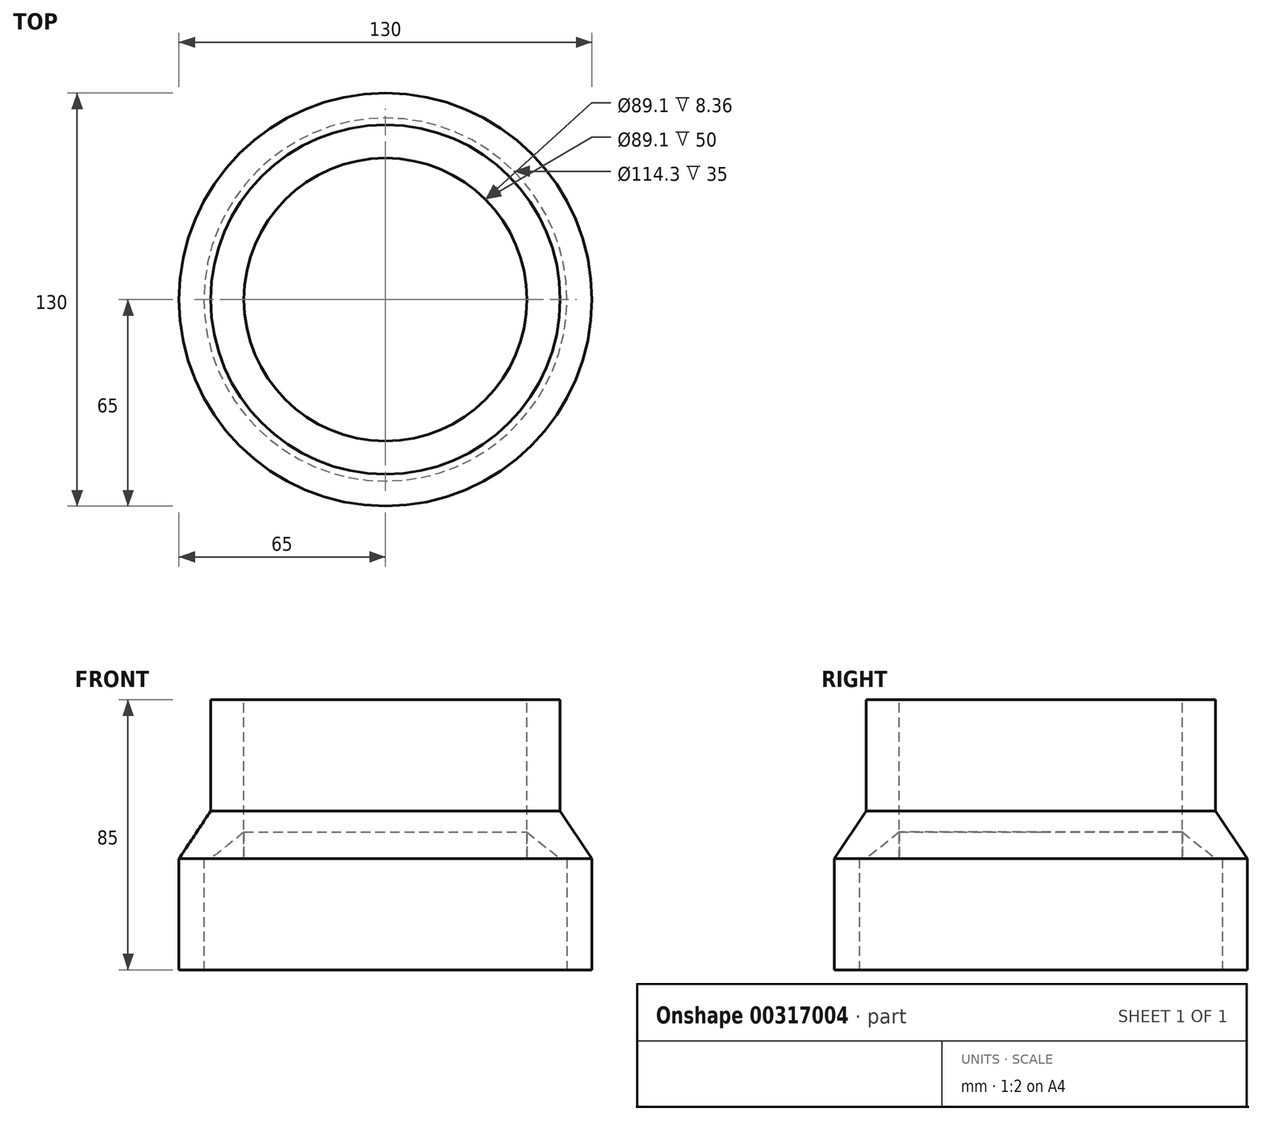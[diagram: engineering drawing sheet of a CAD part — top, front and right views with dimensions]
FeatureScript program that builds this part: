
annotation { "Feature Type Name" : "Feature", "Feature Type Description" : "" }
export const myFeature = defineFeature(function(context is Context, id is Id, definition is map)
    precondition{}
    {
        {
            var Q0;
            Q0=qCreatedBy(makeId("Front.planeOp"),FACE);
            var sketch = newSketch(context, id + "F0", { "sketchPlane" : qUnion([Q0])});
            skLineSegment(sketch, "E0", {"start": v(0, 0) * mm, "end": v(0, 58) * mm});
            skLineSegment(sketch, "E1", {"start": v(0, 58) * mm, "end": v(-25, 58) * mm});
            skLineSegment(sketch, "E2", {"start": v(-25, 58) * mm, "end": v(-25, 43) * mm});
            skLineSegment(sketch, "E3", {"start": v(0, 0) * mm, "end": v(-40, 0) * mm});
            skLineSegment(sketch, "E4", {"start": v(-40, 0) * mm, "end": v(-40, 30) * mm});
            skLineSegment(sketch, "E5", {"start": v(-40, 30) * mm, "end": v(-25, 43) * mm});
            skSolve(sketch);
        }
        {
            var Q0;
            Q0=makeQuery(id+"F0.imprint","IMPRINT",FACE,{"disambiguationData":[TD([[makeQuery(id+"F0.imprint","IMPRINT",EDGE,{"derivedFrom":sQuery(id+"F0.wireOp",EDGE,"E0")}),1.0]])]});
            var Q1;
            Q1=sQuery(id+"F0.wireOp",EDGE,"E0");
            revolve(context, id + "F1", {"entities" : qUnion([Q0]), "axis" : qUnion([Q1]), "revolveType" : RevolveType.FULL});
        }
        {
            var Q0;
            Q0=makeQuery(id+"F1.opRevolve","SWEPT_FACE",FACE,{"disambiguationData":[OSD([sQuery(id+"F0.wireOp",EDGE,"E1")])]});
            var sketch = newSketch(context, id + "F2", { "sketchPlane" : qUnion([Q0])});
            skCircle(sketch, "E6", {"center": v(0, 0) * mm, "radius": 17 * mm});
            skSolve(sketch);
        }
        {
            var Q0;
            Q0=makeQuery(id+"F1.opRevolve","SWEPT_FACE",FACE,{"disambiguationData":[OSD([sQuery(id+"F0.wireOp",EDGE,"E3")])]});
            var sketch = newSketch(context, id + "F3", { "sketchPlane" : qUnion([Q0])});
            skCircle(sketch, "E7", {"center": v(0, 0) * mm, "radius": 30.25 * mm});
            skSolve(sketch);
        }
        {
            var Q0;
            Q0=makeQuery(id+"F2.imprint","IMPRINT",FACE,{"disambiguationData":[TD([[makeQuery(id+"F2.imprint","IMPRINT",EDGE,{"derivedFrom":sQuery(id+"F2.wireOp",EDGE,"E6")}),1.0]])]});
            extrude(context, id + "F4", {"entities" : qUnion([Q0]), "operationType" : NewBodyOperationType.REMOVE, "endBound" : BoundingType.THROUGH_ALL, "oppositeDirection" : true, "depth" : 25 * mm});
        }
        {
            var Q0;
            Q0=makeQuery(id+"F3.imprint","IMPRINT",FACE,{"disambiguationData":[TD([[makeQuery(id+"F3.imprint","IMPRINT",EDGE,{"derivedFrom":sQuery(id+"F3.wireOp",EDGE,"E7")}),1.0]])]});
            extrude(context, id + "F5", {"entities" : qUnion([Q0]), "operationType" : NewBodyOperationType.REMOVE, "oppositeDirection" : true, "depth" : 30 * mm});
        }
        {
            var Q0;
            Q0=qCreatedBy(makeId("Front.planeOp"),FACE);
            var sketch = newSketch(context, id + "F6", { "sketchPlane" : qUnion([Q0])});
            skLineSegment(sketch, "E8", {"start": v(0, 0) * mm, "end": v(0, 72) * mm});
            skLineSegment(sketch, "E9", {"start": v(0, 72) * mm, "end": v(-40, 72) * mm});
            skLineSegment(sketch, "E10", {"start": v(-40, 72) * mm, "end": v(-40, 47) * mm});
            skLineSegment(sketch, "E11", {"start": v(-40, 47) * mm, "end": v(-55, 35) * mm});
            skLineSegment(sketch, "E12", {"start": v(-55, 35) * mm, "end": v(-55, 0) * mm});
            skLineSegment(sketch, "E13", {"start": v(-55, 0) * mm, "end": v(0, 0) * mm});
            skSolve(sketch);
        }
        {
            var Q0;
            Q0 = qSketchRegion(id + "F6", true);
            var Q1;
            Q1=sQuery(id+"F6.wireOp",EDGE,"E8");
            revolve(context, id + "F7", {"entities" : qUnion([Q0]), "axis" : qUnion([Q1]), "revolveType" : RevolveType.FULL});
        }
        {
            var Q0;
            Q0=makeQuery(id+"F7.opRevolve","SWEPT_FACE",FACE,{"disambiguationData":[OSD([sQuery(id+"F6.wireOp",EDGE,"E9")])]});
            var sketch = newSketch(context, id + "F8", { "sketchPlane" : qUnion([Q0])});
            skCircle(sketch, "E14", {"center": v(0, 0) * mm, "radius": 30.25 * mm});
            skSolve(sketch);
        }
        {
            var Q0;
            Q0=makeQuery(id+"F8.imprint","IMPRINT",FACE,{"disambiguationData":[TD([[makeQuery(id+"F8.imprint","IMPRINT",EDGE,{"derivedFrom":sQuery(id+"F8.wireOp",EDGE,"E14")}),1.0]])]});
            extrude(context, id + "F9", {"entities" : qUnion([Q0]), "operationType" : NewBodyOperationType.REMOVE, "endBound" : BoundingType.THROUGH_ALL, "oppositeDirection" : true, "depth" : 25 * mm});
        }
        {
            var Q0;
            Q0=makeQuery(id+"F7.opRevolve","SWEPT_FACE",FACE,{"disambiguationData":[OSD([sQuery(id+"F6.wireOp",EDGE,"E13")])]});
            var sketch = newSketch(context, id + "F10", { "sketchPlane" : qUnion([Q0])});
            skCircle(sketch, "E15", {"center": v(0, 0) * mm, "radius": 44.55 * mm});
            skSolve(sketch);
        }
        {
            var Q0;
            Q0=makeQuery(id+"F10.imprint","IMPRINT",FACE,{"disambiguationData":[TD([[makeQuery(id+"F10.imprint","IMPRINT",EDGE,{"derivedFrom":sQuery(id+"F10.wireOp",EDGE,"E15")}),1.0]])]});
            extrude(context, id + "F11", {"entities" : qUnion([Q0]), "operationType" : NewBodyOperationType.REMOVE, "oppositeDirection" : true, "depth" : 30 * mm});
        }
        {
            var Q0;
            Q0=qCreatedBy(makeId("Front.planeOp"),FACE);
            var sketch = newSketch(context, id + "F12", { "sketchPlane" : qUnion([Q0])});
            skLineSegment(sketch, "E16", {"start": v(0, 0) * mm, "end": v(0, 85) * mm});
            skLineSegment(sketch, "E17", {"start": v(0, 85) * mm, "end": v(-55, 85) * mm});
            skLineSegment(sketch, "E18", {"start": v(-55, 85) * mm, "end": v(-55, 50) * mm});
            skLineSegment(sketch, "E19", {"start": v(-55, 50) * mm, "end": v(-65, 35) * mm});
            skLineSegment(sketch, "E20", {"start": v(-65, 35) * mm, "end": v(-65, 0) * mm});
            skLineSegment(sketch, "E21", {"start": v(-65, 0) * mm, "end": v(0, 0) * mm});
            skSolve(sketch);
        }
        {
            var Q0;
            Q0=makeQuery(id+"F12.imprint","IMPRINT",FACE,{"disambiguationData":[TD([[makeQuery(id+"F12.imprint","IMPRINT",EDGE,{"derivedFrom":sQuery(id+"F12.wireOp",EDGE,"E16")}),1.0]])]});
            var Q1;
            Q1=sQuery(id+"F12.wireOp",EDGE,"E16");
            revolve(context, id + "F13", {"entities" : qUnion([Q0]), "axis" : qUnion([Q1]), "revolveType" : RevolveType.FULL});
        }
        {
            var Q0;
            Q0=makeQuery(id+"F13.opRevolve","SWEPT_FACE",FACE,{"disambiguationData":[OSD([sQuery(id+"F12.wireOp",EDGE,"E17")])]});
            var sketch = newSketch(context, id + "F14", { "sketchPlane" : qUnion([Q0])});
            skCircle(sketch, "E22", {"center": v(0, 0) * mm, "radius": 44.55 * mm});
            skSolve(sketch);
        }
        {
            var Q0;
            Q0=makeQuery(id+"F14.imprint","IMPRINT",FACE,{"disambiguationData":[TD([[makeQuery(id+"F14.imprint","IMPRINT",EDGE,{"derivedFrom":sQuery(id+"F14.wireOp",EDGE,"E22")}),1.0]])]});
            extrude(context, id + "F15", {"entities" : qUnion([Q0]), "operationType" : NewBodyOperationType.REMOVE, "endBound" : BoundingType.THROUGH_ALL, "oppositeDirection" : true, "depth" : 25 * mm});
        }
        {
            var Q0;
            Q0=makeQuery(id+"F13.opRevolve","SWEPT_FACE",FACE,{"disambiguationData":[OSD([sQuery(id+"F12.wireOp",EDGE,"E21")])]});
            var sketch = newSketch(context, id + "F16", { "sketchPlane" : qUnion([Q0])});
            skCircle(sketch, "E23", {"center": v(0, 0) * mm, "radius": 57.15 * mm});
            skSolve(sketch);
        }
        {
            var Q0;
            Q0=makeQuery(id+"F16.imprint","IMPRINT",FACE,{"disambiguationData":[TD([[makeQuery(id+"F16.imprint","IMPRINT",EDGE,{"derivedFrom":sQuery(id+"F16.wireOp",EDGE,"E23")}),1.0]])]});
            extrude(context, id + "F17", {"entities" : qUnion([Q0]), "operationType" : NewBodyOperationType.REMOVE, "oppositeDirection" : true, "depth" : 35 * mm});
        }
    });
